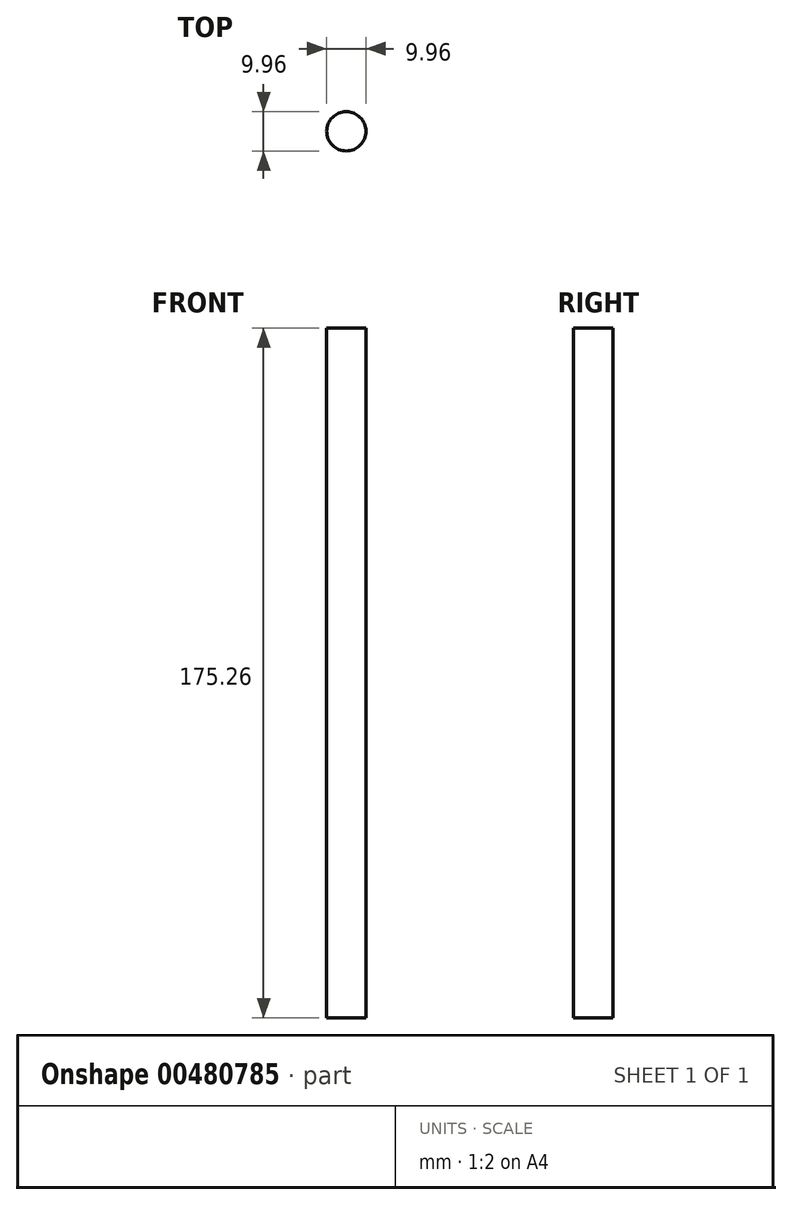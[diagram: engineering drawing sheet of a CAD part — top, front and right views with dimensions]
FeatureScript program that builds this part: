
annotation { "Feature Type Name" : "Feature", "Feature Type Description" : "" }
export const myFeature = defineFeature(function(context is Context, id is Id, definition is map)
    precondition{}
    {
        {
            var Q0;
            Q0=qCreatedBy(makeId("Top.planeOp"),FACE);
            var sketch = newSketch(context, id + "F0", { "sketchPlane" : qUnion([Q0])});
            skCircle(sketch, "E0", {"center": v(0, 0) * mm, "radius": 4.98 * mm});
            skSolve(sketch);
        }
        {
            var Q0;
            Q0=qCreatedBy(makeId("Front.planeOp"),FACE);
            var sketch = newSketch(context, id + "F1", { "sketchPlane" : qUnion([Q0])});
            skLineSegment(sketch, "E1", {"start": v(0, 0) * mm, "end": v(0, -15.6) * mm});
            skSolve(sketch);
        }
        {
            var Q0;
            Q0=makeQuery(id+"F0.imprint","IMPRINT",FACE,{"disambiguationData":[TD([[makeQuery(id+"F0.imprint","IMPRINT",EDGE,{"derivedFrom":sQuery(id+"F0.wireOp",EDGE,"E0")}),1.0]])]});
            var Q1;
            Q1 = qConstructionFilter(qBodyType(qCreatedBy(id + "F1" ,EDGE), BodyType.WIRE), ConstructionObject.NO);
            sweep(context, id + "F2", {"profiles" : qUnion([Q0]), "path" : qUnion([Q1]), "keepProfileOrientation" : true});
        }
        {
            var Q0;
            Q0=makeQuery(id+"F2.opSweep","CAP_FACE",FACE,{"disambiguationData":[OSD([sQuery(id+"F0.wireOp",EDGE,"E0"),sQuery(id+"F1.wireOp",VERTEX,"E1.end")])],"isStart":false});
            extrude(context, id + "F3", {"entities" : qUnion([Q0]), "operationType" : NewBodyOperationType.ADD, "oppositeDirection" : true, "depth" : 175.26 * mm});
        }
    });
